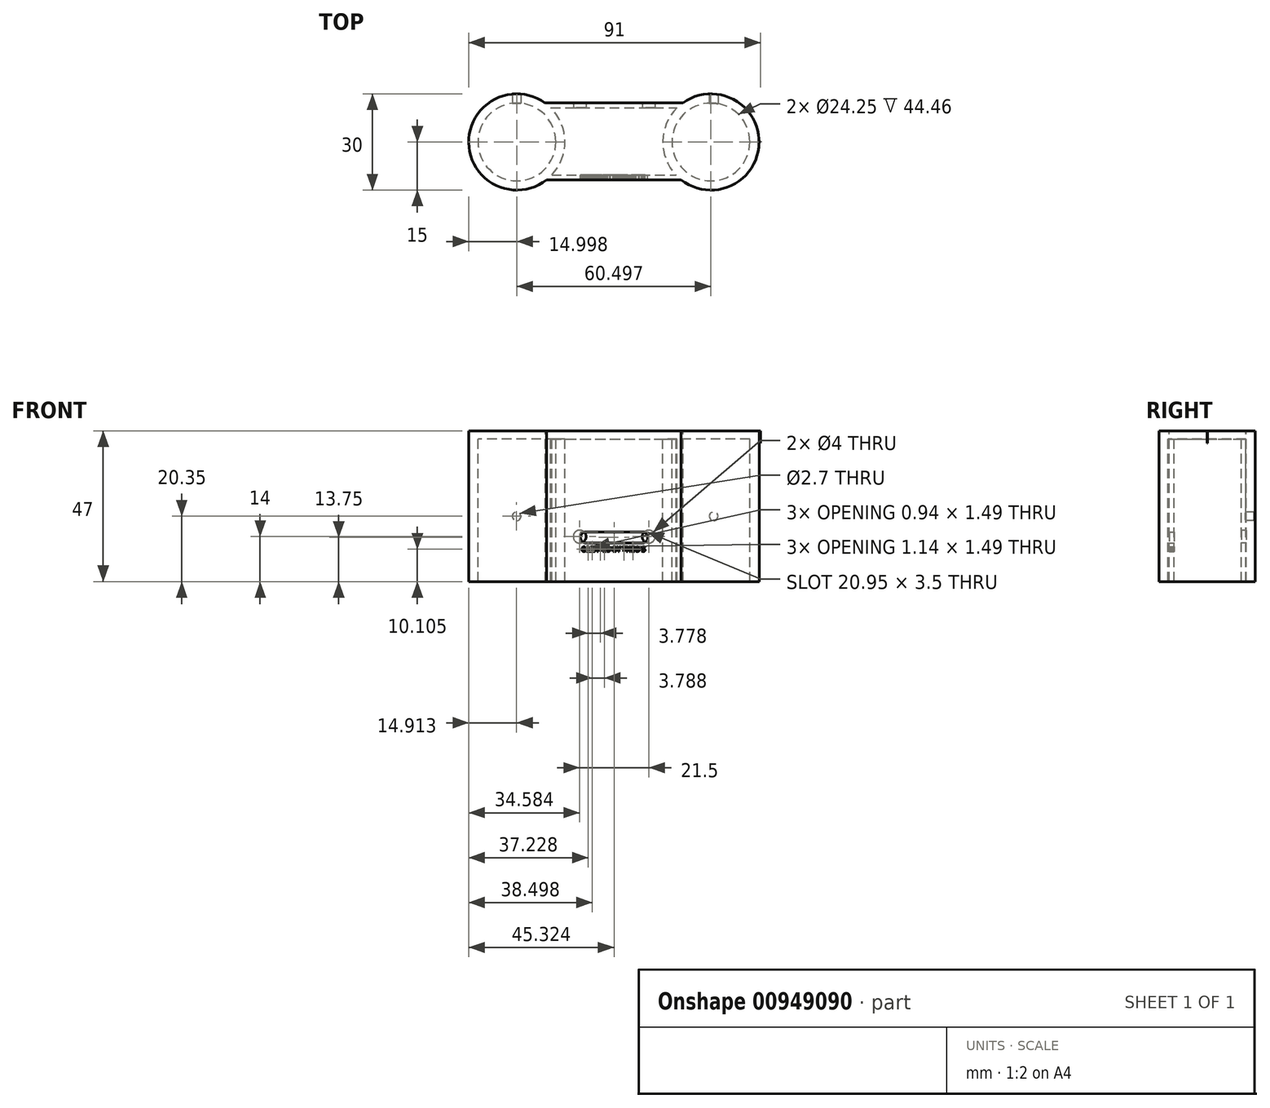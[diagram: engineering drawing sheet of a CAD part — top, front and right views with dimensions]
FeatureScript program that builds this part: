
annotation { "Feature Type Name" : "Feature", "Feature Type Description" : "" }
export const myFeature = defineFeature(function(context is Context, id is Id, definition is map)
    precondition{}
    {
        {
            var Q0;
            Q0=qCreatedBy(makeId("Top.planeOp"),FACE);
            var sketch = newSketch(context, id + "F0", { "sketchPlane" : qUnion([Q0])});
            skLineSegment(sketch, "E0.bottom", {"start": v(-28.9, -11.78) * mm, "end": v(14.1, -11.78) * mm});
            skLineSegment(sketch, "E0.top", {"start": v(-28.9, 12.22) * mm, "end": v(14.1, 12.22) * mm});
            skLineSegment(sketch, "E0.left", {"start": v(-28.9, -11.78) * mm, "end": v(-28.9, 12.22) * mm});
            skLineSegment(sketch, "E0.right", {"start": v(14.1, -11.78) * mm, "end": v(14.1, 12.22) * mm});
            skLineSegment(sketch, "E1.bottom", {"start": v(-27.69, -10.32) * mm, "end": v(12.81, -10.32) * mm});
            skLineSegment(sketch, "E1.top", {"start": v(-27.69, 10.68) * mm, "end": v(12.81, 10.68) * mm});
            skLineSegment(sketch, "E1.left", {"start": v(-27.69, -10.32) * mm, "end": v(-27.69, 10.68) * mm});
            skLineSegment(sketch, "E1.right", {"start": v(12.81, -10.32) * mm, "end": v(12.81, 10.68) * mm});
            skCircle(sketch, "E2", {"center": v(-37.75, 0) * mm, "radius": 12.12 * mm});
            skCircle(sketch, "E3", {"center": v(-37.75, 0) * mm, "radius": 15 * mm});
            skCircle(sketch, "E4", {"center": v(22.75, 0) * mm, "radius": 15 * mm});
            skCircle(sketch, "E5", {"center": v(22.75, 0) * mm, "radius": 12.12 * mm});
            skLineSegment(sketch, "E6.bottom", {"start": v(-52.75, -15) * mm, "end": v(37.74, -15) * mm});
            skLineSegment(sketch, "E6.top", {"start": v(-52.75, 15) * mm, "end": v(37.74, 15) * mm});
            skLineSegment(sketch, "E6.left", {"start": v(-52.75, -15) * mm, "end": v(-52.75, 15) * mm});
            skLineSegment(sketch, "E6.right", {"start": v(37.74, -15) * mm, "end": v(37.74, 15) * mm});
            skPoint(sketch, "E7", {"position": v(-41.75, -11.5) * mm});
            skSolve(sketch);
        }
        {
            var Q0;
            {var subQ7=sQuery(id+"F0.wireOp",EDGE,"E0.left");var subQ8=sQuery(id+"F0.wireOp",EDGE,"E0.bottom");var subQ9=makeQuery(id+"F0.imprint","INTERSECT",VERTEX,{"derivedFrom":[subQ8,subQ7]});Q0=makeQuery(id+"F0.imprint","IMPRINT",FACE,{"disambiguationData":[TD([[makeQuery(id+"F0.imprint","IMPRINT",EDGE,{"disambiguationData":[TD([[subQ9,-1.0]])],"derivedFrom":subQ8}),1.0]])]});}
            var Q1;
            {var subQ1=sQuery(id+"F0.wireOp",EDGE,"E0.left");var subQ5=sQuery(id+"F0.wireOp",EDGE,"E0.bottom");var subQ8=makeQuery(id+"F0.imprint","INTERSECT",VERTEX,{"derivedFrom":[subQ5,subQ1]});Q1=makeQuery(id+"F0.imprint","IMPRINT",FACE,{"disambiguationData":[TD([[makeQuery(id+"F0.imprint","IMPRINT",EDGE,{"disambiguationData":[TD([[subQ8,-1.0]])],"derivedFrom":subQ5}),-1.0]])]});}
            var Q2;
            {var subQ0=sQuery(id+"F0.wireOp",EDGE,"E1.left");var subQ1=sQuery(id+"F0.wireOp",EDGE,"E1.bottom");var subQ2=makeQuery(id+"F0.imprint","INTERSECT",VERTEX,{"derivedFrom":[subQ1,subQ0]});Q2=makeQuery(id+"F0.imprint","IMPRINT",FACE,{"disambiguationData":[TD([[makeQuery(id+"F0.imprint","IMPRINT",EDGE,{"disambiguationData":[TD([[subQ2,-1.0]])],"derivedFrom":subQ1}),1.0]])]});}
            var Q3;
            {var subQ1=sQuery(id+"F0.wireOp",EDGE,"E0.left");var subQ7=sQuery(id+"F0.wireOp",EDGE,"E3");var subQ9=makeQuery(id+"F0.imprint","INTERSECT",VERTEX,{"derivedFrom":[subQ1,subQ7]});Q3=makeQuery(id+"F0.imprint","IMPRINT",FACE,{"disambiguationData":[TD([[makeQuery(id+"F0.imprint","IMPRINT",EDGE,{"disambiguationData":[TD([[subQ9,1.0]])],"derivedFrom":subQ1}),-1.0]])]});}
            var Q4;
            {var subQ0=sQuery(id+"F0.wireOp",EDGE,"E1.right");var subQ5=sQuery(id+"F0.wireOp",EDGE,"E1.bottom");var subQ6=makeQuery(id+"F0.imprint","INTERSECT",VERTEX,{"derivedFrom":[subQ5,subQ0]});Q4=makeQuery(id+"F0.imprint","IMPRINT",FACE,{"disambiguationData":[TD([[makeQuery(id+"F0.imprint","IMPRINT",EDGE,{"disambiguationData":[TD([[subQ6,1.0]])],"derivedFrom":subQ5}),1.0]])]});}
            var Q5;
            {var subQ7=sQuery(id+"F0.wireOp",EDGE,"E0.right");var subQ8=sQuery(id+"F0.wireOp",EDGE,"E0.bottom");var subQ9=makeQuery(id+"F0.imprint","INTERSECT",VERTEX,{"derivedFrom":[subQ8,subQ7]});Q5=makeQuery(id+"F0.imprint","IMPRINT",FACE,{"disambiguationData":[TD([[makeQuery(id+"F0.imprint","IMPRINT",EDGE,{"disambiguationData":[TD([[subQ9,1.0]])],"derivedFrom":subQ8}),1.0]])]});}
            var Q6;
            {var subQ0=sQuery(id+"F0.wireOp",EDGE,"E0.right");var subQ5=sQuery(id+"F0.wireOp",EDGE,"E0.bottom");var subQ6=makeQuery(id+"F0.imprint","INTERSECT",VERTEX,{"derivedFrom":[subQ5,subQ0]});Q6=makeQuery(id+"F0.imprint","IMPRINT",FACE,{"disambiguationData":[TD([[makeQuery(id+"F0.imprint","IMPRINT",EDGE,{"disambiguationData":[TD([[subQ6,1.0]])],"derivedFrom":subQ5}),-1.0]])]});}
            var Q7;
            {var subQ7=sQuery(id+"F0.wireOp",EDGE,"E0.right");var subQ8=sQuery(id+"F0.wireOp",EDGE,"E0.top");var subQ9=makeQuery(id+"F0.imprint","INTERSECT",VERTEX,{"derivedFrom":[subQ8,subQ7]});Q7=makeQuery(id+"F0.imprint","IMPRINT",FACE,{"disambiguationData":[TD([[makeQuery(id+"F0.imprint","IMPRINT",EDGE,{"disambiguationData":[TD([[subQ9,1.0]])],"derivedFrom":subQ8}),-1.0]])]});}
            var Q8;
            {var subQ0=sQuery(id+"F0.wireOp",EDGE,"E3");var subQ1=sQuery(id+"F0.wireOp",EDGE,"E0.bottom");var subQ2=makeQuery(id+"F0.imprint","INTERSECT",VERTEX,{"derivedFrom":[subQ1,subQ0]});Q8=makeQuery(id+"F0.imprint","IMPRINT",FACE,{"disambiguationData":[TD([[makeQuery(id+"F0.imprint","IMPRINT",EDGE,{"disambiguationData":[TD([[subQ2,-1.0]])],"derivedFrom":subQ1}),1.0]])]});}
            var Q9;
            {var subQ5=sQuery(id+"F0.wireOp",EDGE,"E0.left");var subQ7=sQuery(id+"F0.wireOp",EDGE,"E0.top");var subQ8=makeQuery(id+"F0.imprint","INTERSECT",VERTEX,{"derivedFrom":[subQ7,subQ5]});Q9=makeQuery(id+"F0.imprint","IMPRINT",FACE,{"disambiguationData":[TD([[makeQuery(id+"F0.imprint","IMPRINT",EDGE,{"disambiguationData":[TD([[subQ8,-1.0]])],"derivedFrom":subQ7}),-1.0]])]});}
            extrude(context, id + "F1", {"entities" : qUnion([Q0, Q1, Q2, Q3, Q4, Q5, Q6, Q7, Q8, Q9]), "depth" : 47 * mm, "offsetDistance" : 25.4 * mm});
        }
        {
            var Q0;
            {var subQ0=sQuery(id+"F0.wireOp",EDGE,"E2");var subQ1=sQuery(id+"F0.wireOp",EDGE,"E0.left");var subQ2=makeQuery(id+"F0.imprint","INTERSECT",VERTEX,{"disambiguationData":[OD(0.0)],"derivedFrom":[subQ1,subQ0]});Q0=makeQuery(id+"F0.imprint","IMPRINT",FACE,{"disambiguationData":[TD([[makeQuery(id+"F0.imprint","IMPRINT",EDGE,{"disambiguationData":[TD([[subQ2,-1.0]])],"derivedFrom":subQ1}),1.0]])]});}
            var Q1;
            {var subQ0=sQuery(id+"F0.wireOp",EDGE,"E2");var subQ1=sQuery(id+"F0.wireOp",EDGE,"E1.left");var subQ2=makeQuery(id+"F0.imprint","INTERSECT",VERTEX,{"disambiguationData":[OD(0.0)],"derivedFrom":[subQ1,subQ0]});Q1=makeQuery(id+"F0.imprint","IMPRINT",FACE,{"disambiguationData":[TD([[makeQuery(id+"F0.imprint","IMPRINT",EDGE,{"disambiguationData":[TD([[subQ2,-1.0]])],"derivedFrom":subQ1}),-1.0]])]});}
            var Q2;
            {var subQ0=sQuery(id+"F0.wireOp",EDGE,"E3");var subQ1=sQuery(id+"F0.wireOp",EDGE,"E1.bottom");var subQ2=makeQuery(id+"F0.imprint","INTERSECT",VERTEX,{"derivedFrom":[subQ1,subQ0]});Q2=makeQuery(id+"F0.imprint","IMPRINT",FACE,{"disambiguationData":[TD([[makeQuery(id+"F0.imprint","IMPRINT",EDGE,{"disambiguationData":[TD([[subQ2,-1.0]])],"derivedFrom":subQ1}),1.0]])]});}
            var Q3;
            {var subQ0=sQuery(id+"F0.wireOp",EDGE,"E5");var subQ1=sQuery(id+"F0.wireOp",EDGE,"E1.right");var subQ2=makeQuery(id+"F0.imprint","INTERSECT",VERTEX,{"disambiguationData":[OD(0.0)],"derivedFrom":[subQ1,subQ0]});Q3=makeQuery(id+"F0.imprint","IMPRINT",FACE,{"disambiguationData":[TD([[makeQuery(id+"F0.imprint","IMPRINT",EDGE,{"disambiguationData":[TD([[subQ2,-1.0]])],"derivedFrom":subQ1}),1.0]])]});}
            var Q4;
            {var subQ0=sQuery(id+"F0.wireOp",EDGE,"E5");var subQ1=sQuery(id+"F0.wireOp",EDGE,"E0.right");var subQ2=makeQuery(id+"F0.imprint","INTERSECT",VERTEX,{"disambiguationData":[OD(0.0)],"derivedFrom":[subQ1,subQ0]});Q4=makeQuery(id+"F0.imprint","IMPRINT",FACE,{"disambiguationData":[TD([[makeQuery(id+"F0.imprint","IMPRINT",EDGE,{"disambiguationData":[TD([[subQ2,-1.0]])],"derivedFrom":subQ1}),1.0]])]});}
            var Q5;
            {var subQ0=sQuery(id+"F0.wireOp",EDGE,"E2");var subQ1=sQuery(id+"F0.wireOp",EDGE,"E0.left");var subQ2=makeQuery(id+"F0.imprint","INTERSECT",VERTEX,{"disambiguationData":[OD(0.0)],"derivedFrom":[subQ1,subQ0]});Q5=makeQuery(id+"F0.imprint","IMPRINT",FACE,{"disambiguationData":[TD([[makeQuery(id+"F0.imprint","IMPRINT",EDGE,{"disambiguationData":[TD([[subQ2,-1.0]])],"derivedFrom":subQ1}),-1.0]])]});}
            var Q6;
            {var subQ0=sQuery(id+"F0.wireOp",EDGE,"E5");var subQ1=sQuery(id+"F0.wireOp",EDGE,"E0.right");var subQ2=makeQuery(id+"F0.imprint","INTERSECT",VERTEX,{"disambiguationData":[OD(0.0)],"derivedFrom":[subQ1,subQ0]});Q6=makeQuery(id+"F0.imprint","IMPRINT",FACE,{"disambiguationData":[TD([[makeQuery(id+"F0.imprint","IMPRINT",EDGE,{"disambiguationData":[TD([[subQ2,-1.0]])],"derivedFrom":subQ1}),-1.0]])]});}
            extrude(context, id + "F2", {"entities" : qUnion([Q0, Q1, Q2, Q3, Q4, Q5, Q6]), "operationType" : NewBodyOperationType.ADD, "depth" : 2.54 * mm, "offsetDistance" : 25.4 * mm});
        }
        {
            var Q0;
            Q0=makeQuery(id+"F1.opExtrude","SWEPT_BODY",BODY,{"disambiguationData":[OSD([sQuery(id+"F0.wireOp",EDGE,"E0.bottom"),sQuery(id+"F0.wireOp",EDGE,"E0.top"),sQuery(id+"F0.wireOp",EDGE,"E0.left"),sQuery(id+"F0.wireOp",EDGE,"E1.bottom"),sQuery(id+"F0.wireOp",EDGE,"E1.top"),sQuery(id+"F0.wireOp",EDGE,"E2"),sQuery(id+"F0.wireOp",EDGE,"E3"),sQuery(id+"F0.wireOp",EDGE,"E4"),sQuery(id+"F0.wireOp",EDGE,"E5")])]});
            var Q1;
            Q1=qCreatedBy(makeId("Top.planeOp"),FACE);
            mirror(context, id + "F3", {"entities" : qUnion([Q0]), "mirrorPlane" : qUnion([Q1])});
        }
        {
            var Q0;
            Q0=makeQuery(id+"F1.opExtrude","SWEPT_BODY",BODY,{"disambiguationData":[OSD([sQuery(id+"F0.wireOp",EDGE,"E0.bottom"),sQuery(id+"F0.wireOp",EDGE,"E0.top"),sQuery(id+"F0.wireOp",EDGE,"E0.left"),sQuery(id+"F0.wireOp",EDGE,"E1.bottom"),sQuery(id+"F0.wireOp",EDGE,"E1.top"),sQuery(id+"F0.wireOp",EDGE,"E2"),sQuery(id+"F0.wireOp",EDGE,"E3"),sQuery(id+"F0.wireOp",EDGE,"E4"),sQuery(id+"F0.wireOp",EDGE,"E5")])]});
            deleteBodies(context, id + "F4", {"entities" : qUnion([Q0])});
        }
        {
            var Q0;
            Q0=qCreatedBy(makeId("Front.planeOp"),FACE);
            var sketch = newSketch(context, id + "F5", { "sketchPlane" : qUnion([Q0])});
            skLineSegment(sketch, "E8.bottom", {"start": v(3.05, -31.5) * mm, "end": v(-17.9, -31.5) * mm});
            skLineSegment(sketch, "E8.top", {"start": v(3.05, -35) * mm, "end": v(-17.9, -35) * mm});
            skLineSegment(sketch, "E8.left", {"start": v(3.05, -31.5) * mm, "end": v(3.05, -35) * mm});
            skLineSegment(sketch, "E8.right", {"start": v(-17.9, -31.5) * mm, "end": v(-17.9, -35) * mm});
            skCircle(sketch, "E9", {"center": v(1.3, -33.25) * mm, "radius": 1.75 * mm});
            skCircle(sketch, "E10", {"center": v(-16.15, -33.25) * mm, "radius": 1.75 * mm});
            skSolve(sketch);
        }
        {
            var Q0;
            {var subQ0=sQuery(id+"F5.wireOp",EDGE,"E9");var subQ1=makeQuery(id+"F5.imprint","INTERSECT",VERTEX,{"derivedFrom":[sQuery(id+"F5.wireOp",EDGE,"E8.bottom"),subQ0]});Q0=makeQuery(id+"F5.imprint","IMPRINT",FACE,{"disambiguationData":[TD([[makeQuery(id+"F5.imprint","IMPRINT",EDGE,{"disambiguationData":[TD([[subQ1,1.0]])],"derivedFrom":subQ0}),1.0]])]});}
            var Q1;
            {var subQ0=sQuery(id+"F5.wireOp",EDGE,"E9");var subQ1=sQuery(id+"F5.wireOp",EDGE,"E8.bottom");var subQ2=makeQuery(id+"F5.imprint","INTERSECT",VERTEX,{"derivedFrom":[subQ1,subQ0]});Q1=makeQuery(id+"F5.imprint","IMPRINT",FACE,{"disambiguationData":[TD([[makeQuery(id+"F5.imprint","IMPRINT",EDGE,{"disambiguationData":[TD([[subQ2,-1.0]])],"derivedFrom":subQ1}),1.0]])]});}
            var Q2;
            {var subQ0=sQuery(id+"F5.wireOp",EDGE,"E10");var subQ1=makeQuery(id+"F5.imprint","INTERSECT",VERTEX,{"derivedFrom":[sQuery(id+"F5.wireOp",EDGE,"E8.bottom"),subQ0]});Q2=makeQuery(id+"F5.imprint","IMPRINT",FACE,{"disambiguationData":[TD([[makeQuery(id+"F5.imprint","IMPRINT",EDGE,{"disambiguationData":[TD([[subQ1,-1.0]])],"derivedFrom":subQ0}),1.0]])]});}
            extrude(context, id + "F6", {"entities" : qUnion([Q0, Q1, Q2]), "operationType" : NewBodyOperationType.REMOVE, "depth" : 25.4 * mm, "offsetDistance" : 25.4 * mm});
        }
        {
            var Q0;
            Q0=qCreatedBy(makeId("Front.planeOp"),FACE);
            var sketch = newSketch(context, id + "F7", { "sketchPlane" : qUnion([Q0])});
            skCircle(sketch, "E11", {"center": v(3.33, -33) * mm, "radius": 2 * mm});
            skCircle(sketch, "E12", {"center": v(-18.17, -33) * mm, "radius": 2 * mm});
            skLineSegment(sketch, "E13", {"start": v(3.33, -33) * mm, "end": v(-18.17, -33) * mm});
            skPoint(sketch, "E14", {"position": v(-16.17, -33) * mm});
            skPoint(sketch, "E15", {"position": v(1.33, -33) * mm});
            skSolve(sketch);
        }
        {
            var Q0;
            Q0 = qSketchRegion(id + "F7", true);
            extrude(context, id + "F8", {"entities" : qUnion([Q0]), "operationType" : NewBodyOperationType.REMOVE, "oppositeDirection" : true, "depth" : 25.4 * mm, "offsetDistance" : 25.4 * mm});
        }
        {
            var Q0;
            Q0=qCreatedBy(makeId("Front.planeOp"),FACE);
            var sketch = newSketch(context, id + "F9", { "sketchPlane" : qUnion([Q0])});
            skCircle(sketch, "E16", {"center": v(-37.84, -26.65) * mm, "radius": 1.35 * mm});
            skCircle(sketch, "E17", {"center": v(23.58, -26.65) * mm, "radius": 1.35 * mm});
            skSolve(sketch);
        }
        {
            var Q0;
            Q0 = qSketchRegion(id + "F9", true);
            extrude(context, id + "F10", {"entities" : qUnion([Q0]), "operationType" : NewBodyOperationType.REMOVE, "oppositeDirection" : true, "depth" : 36.58 * mm, "offsetDistance" : 25.4 * mm});
        }
        {
            var Q0;
            Q0=qCreatedBy(makeId("Front.planeOp"),FACE);
            var sketch = newSketch(context, id + "F11", { "sketchPlane" : qUnion([Q0])});
            skText(sketch, "E18", { "text": "CREATED BY THEO S", "fontName": "NotoSansCJKjp-Bold.otf"});
            const initialGuessF11  = {"E18": [-0.0176, -0.03764, 1, 0, 0.00145]};
            skSetInitialGuess(sketch, initialGuessF11);
            skSolve(sketch);
        }
        {
            var Q0;
            Q0 = qSketchRegion(id + "F11", true);
            extrude(context, id + "F12", {"entities" : qUnion([Q0]), "operationType" : NewBodyOperationType.REMOVE, "depth" : 19.8 * mm, "offsetDistance" : 25.4 * mm});
        }
        {
            var Q0;
            Q0=qCreatedBy(makeId("Top.planeOp"),FACE);
            var sketch = newSketch(context, id + "F13", { "sketchPlane" : qUnion([Q0])});
            skLineSegment(sketch, "E19", {"start": v(38.25, 0) * mm, "end": v(37.74, 0) * mm});
            skLineSegment(sketch, "E20", {"start": v(37.74, 0.12) * mm, "end": v(38.25, 0.12) * mm});
            skLineSegment(sketch, "E21", {"start": v(38.25, 0.12) * mm, "end": v(38.25, 0) * mm});
            skLineSegment(sketch, "E22", {"start": v(37.74, 0.12) * mm, "end": v(37.74, 0) * mm});
            skSolve(sketch);
        }
        {
            var Q0;
            Q0 = qSketchRegion(id + "F13", true);
            extrude(context, id + "F14", {"entities" : qUnion([Q0]), "oppositeDirection" : true, "depth" : 3.8 * mm, "offsetDistance" : 25.4 * mm});
        }
    });
